FCSTD DOCUMENT  (FreeCAD 1.1R39228 (Git))
Label: hackrf (new)
License: All rights reserved
LicenseURL: https://en.wikipedia.org/wiki/All_rights_reserved
objects: Sketcher::SketchObject×1, PartDesign::Body×1
note: 3 computed .brp shape members not serialized (recipe doc carries the construction recipe); baked Part::Feature solids carry a one-line shape summary decoded from their .brp

FEATURE [Sketcher::SketchObject] Sketch
  ArcFitTolerance = 1e-06
  AttachmentSupport = -> [XY_Plane]
  FullyConstrained = true
  MakeInternals = false
  MapMode = 5
  sketch-geometry (26):
    g0: Circle CenterX=-33.5 CenterY=55.835 CenterZ=0 NormalX=0 NormalY=0 NormalZ=1 AngleXU=0 Radius=1.7
    g1: Circle CenterX=33.5 CenterY=55.835 CenterZ=0 NormalX=0 NormalY=0 NormalZ=1 AngleXU=0 Radius=1.7
    g2: LineSegment [constr] StartX=-35.2 StartY=55.835 StartZ=0 EndX=35.2 EndY=55.835 EndZ=0
    g3: GeomPoint [constr] X=-35.2 Y=55.835 Z=0
    g4: GeomPoint [constr] X=35.2 Y=55.835 Z=0
    g5: Circle CenterX=-6.43685 CenterY=10.7896 CenterZ=0 NormalX=0 NormalY=0 NormalZ=1 AngleXU=0 Radius=1.7
    g6: Circle CenterX=33.5 CenterY=5.895 CenterZ=0 NormalX=0 NormalY=0 NormalZ=1 AngleXU=0 Radius=1.7
    g7: Circle CenterX=33.5 CenterY=-55.835 CenterZ=0 NormalX=0 NormalY=0 NormalZ=1 AngleXU=0 Radius=1.7
    g8: Circle CenterX=-33.5 CenterY=-55.835 CenterZ=0 NormalX=0 NormalY=0 NormalZ=1 AngleXU=0 Radius=1.7
    g9: GeomPoint [constr] X=-34.3755 Y=57.2922 Z=0
    g10: GeomPoint [constr] X=-5.56135 Y=9.33237 Z=0
    g11: LineSegment [constr] StartX=-34.3755 StartY=57.2922 StartZ=0 EndX=-5.56135 EndY=9.33237 EndZ=0
    g12: GeomPoint [constr] X=-7.56463 Y=9.51755 Z=0
    g13: LineSegment [constr] StartX=34.6278 StartY=57.107 StartZ=0 EndX=-7.56463 EndY=9.51755 EndZ=0
    g14: GeomPoint [constr] X=34.6278 Y=57.107 Z=0
    g15: LineSegment [constr] StartX=33.5 StartY=57.535 StartZ=0 EndX=33.5 EndY=-57.535 EndZ=0
    g16: GeomPoint [constr] X=33.5 Y=57.535 Z=0
    g17: GeomPoint [constr] X=33.5 Y=4.195 Z=0
    g18: GeomPoint [constr] X=33.5 Y=-57.535 Z=0
    g19: GeomPoint [constr] X=33.5 Y=7.595 Z=0
    g20: LineSegment [constr] StartX=35.2 StartY=-55.835 StartZ=0 EndX=-31.8 EndY=-55.835 EndZ=0
    g21: LineSegment [constr] StartX=-33.5 StartY=57.535 StartZ=0 EndX=-33.5 EndY=-54.135 EndZ=0
    g22: LineSegment [constr] StartX=-8.12422 StartY=10.9964 StartZ=0 EndX=35.1874 EndY=5.6882 EndZ=0
    g23: GeomPoint [constr] X=35.1874 Y=5.6882 Z=0
    g24: GeomPoint [constr] X=-8.12422 Y=10.9964 Z=0
    g25: GeomPoint X=0 Y=0 Z=0
  constraints (61):
    c: Diameter(g0) = 3.4
    c: Horizontal(g2)
    c: PointOnObject(g0,g2)
    c: PointOnObject(g1,g2)
    c: Equal(g1,g0)
    c: DistanceX(g3,g4) = 70.4
    c: Equal(g6,g0)
    c: Equal(g5,g0)
    c: Equal(g7,g0)
    c: Equal(g8,g0)
    c: PointOnObject(g0,g11)
    c: PointOnObject(g5,g11)
    c: Distance(g10,g9) = 55.95
    c: PointOnObject(g5,g13)
    c: PointOnObject(g1,g13)
    c: Distance(g12,g14) = 63.6
    c: Vertical(g15)
    c: PointOnObject(g1,g15)
    c: Distance(g17,g16) = 53.34
    c: PointOnObject(g7,g15)
    c: Distance(g18,g19) = 65.13
    c: Horizontal(g20)
    c: PointOnObject(g7,g20)
    c: PointOnObject(g8,g20)
    c: Vertical(g21)
    c: PointOnObject(g8,g21)
    c: PointOnObject(g0,g21)
    c: PointOnObject(g5,g22)
    c: Coincident(g13,g14)
    c: Coincident(g13,g12)
    c: PointOnObject(g12,g5)
    c: Coincident(g11,g10)
    c: PointOnObject(g10,g5)
    c: Coincident(g22,g24)
    c: PointOnObject(g22,g5)
    c: Coincident(g11,g9)
    c: PointOnObject(g21,g0)
    c: Coincident(g2,g3)
    c: PointOnObject(g2,g0)
    c: PointOnObject(g9,g0)
    c: PointOnObject(g15,g1)
    c: PointOnObject(g13,g1)
    c: Coincident(g2,g4)
    c: PointOnObject(g2,g1)
    c: Coincident(g22,g23)
    c: Coincident(g18,g15)
    c: PointOnObject(g15,g7)
    c: PointOnObject(g20,g7)
    c: PointOnObject(g20,g8)
    c: PointOnObject(g21,g8)
    c: Coincident(g16,g15)
    c: Distance(g22,g22) = 43.6357
    c: PointOnObject(g6,g15)
    c: PointOnObject(g6,g22)
    c: PointOnObject(g22,g6)
    c: PointOnObject(g17,g6)
    c: PointOnObject(g17,g15)
    c: PointOnObject(g19,g6)
    c: PointOnObject(g19,g15)
    c: Symmetric(g1,g8,g25)
    c: Coincident(g25,g-1)
FEATURE [PartDesign::Body] Body
  AllowCompound = false
  Group = -> [Sketch]
  Origin = -> Origin
